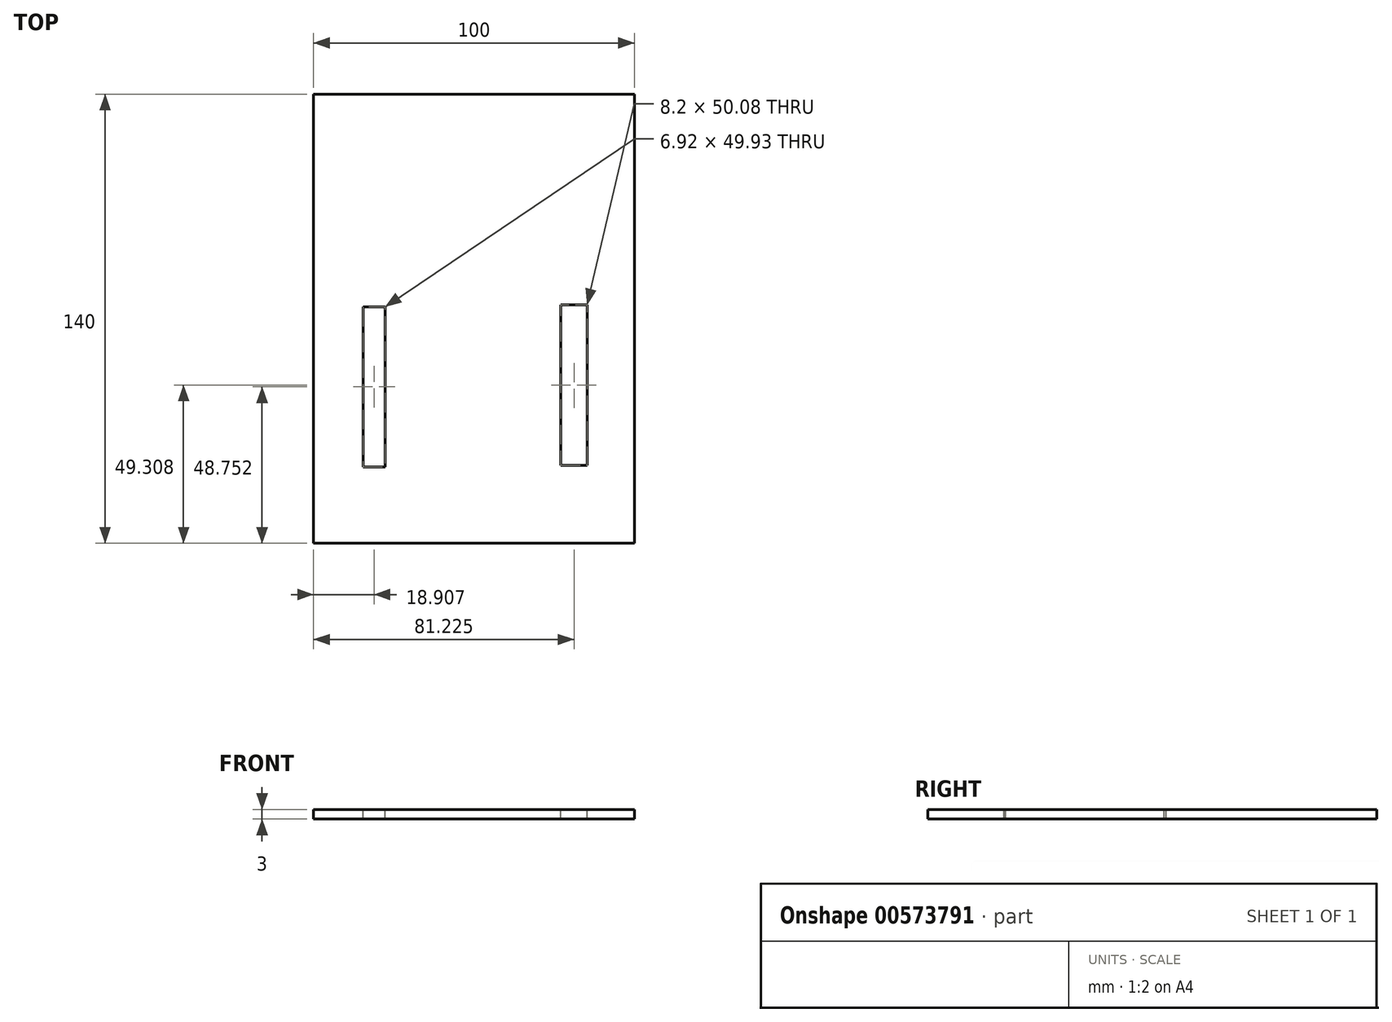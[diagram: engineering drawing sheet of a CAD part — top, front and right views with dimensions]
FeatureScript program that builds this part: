
annotation { "Feature Type Name" : "Feature", "Feature Type Description" : "" }
export const myFeature = defineFeature(function(context is Context, id is Id, definition is map)
    precondition{}
    {
        {
            var Q0;
            Q0=qCreatedBy(makeId("Top.planeOp"),FACE);
            var sketch = newSketch(context, id + "F0", { "sketchPlane" : qUnion([Q0])});
            skLineSegment(sketch, "E0.bottom", {"start": v(0, 0) * mm, "end": v(-100, 0) * mm});
            skLineSegment(sketch, "E0.top", {"start": v(0, 140) * mm, "end": v(-100, 140) * mm});
            skLineSegment(sketch, "E0.left", {"start": v(0, 0) * mm, "end": v(0, 140) * mm});
            skLineSegment(sketch, "E0.right", {"start": v(-100, 0) * mm, "end": v(-100, 140) * mm});
            skSolve(sketch);
        }
        {
            var Q0;
            Q0=makeQuery(id+"F0.imprint","IMPRINT",FACE,{"disambiguationData":[TD([[makeQuery(id+"F0.imprint","IMPRINT",EDGE,{"derivedFrom":sQuery(id+"F0.wireOp",EDGE,"E0.bottom")}),-1.0]])]});
            extrude(context, id + "F1", {"entities" : qUnion([Q0]), "depth" : 3 * mm, "offsetDistance" : 25 * mm});
        }
        {
            var Q0;
            Q0=makeQuery(id+"F1.opExtrude","CAP_FACE",FACE,{"disambiguationData":[OSD([sQuery(id+"F0.wireOp",EDGE,"E0.bottom"),sQuery(id+"F0.wireOp",EDGE,"E0.top"),sQuery(id+"F0.wireOp",EDGE,"E0.left"),sQuery(id+"F0.wireOp",EDGE,"E0.right")])],"isStart":false});
            var sketch = newSketch(context, id + "F2", { "sketchPlane" : qUnion([Q0])});
            skLineSegment(sketch, "E1.bottom", {"start": v(-84.55, 73.72) * mm, "end": v(-77.63, 73.72) * mm});
            skLineSegment(sketch, "E1.top", {"start": v(-84.55, 23.79) * mm, "end": v(-77.63, 23.79) * mm});
            skLineSegment(sketch, "E1.left", {"start": v(-84.55, 73.72) * mm, "end": v(-84.55, 23.79) * mm});
            skLineSegment(sketch, "E1.right", {"start": v(-77.63, 73.72) * mm, "end": v(-77.63, 23.79) * mm});
            skLineSegment(sketch, "E2.bottom", {"start": v(-22.87, 74.35) * mm, "end": v(-14.68, 74.35) * mm});
            skLineSegment(sketch, "E2.top", {"start": v(-22.87, 24.27) * mm, "end": v(-14.68, 24.27) * mm});
            skLineSegment(sketch, "E2.left", {"start": v(-22.87, 74.35) * mm, "end": v(-22.87, 24.27) * mm});
            skLineSegment(sketch, "E2.right", {"start": v(-14.68, 74.35) * mm, "end": v(-14.68, 24.27) * mm});
            skSolve(sketch);
        }
        {
            var Q0;
            Q0 = qSketchRegion(id + "F2", true);
            extrude(context, id + "F3", {"entities" : qUnion([Q0]), "operationType" : NewBodyOperationType.REMOVE, "oppositeDirection" : true, "depth" : 25 * mm, "offsetDistance" : 25 * mm});
        }
    });
